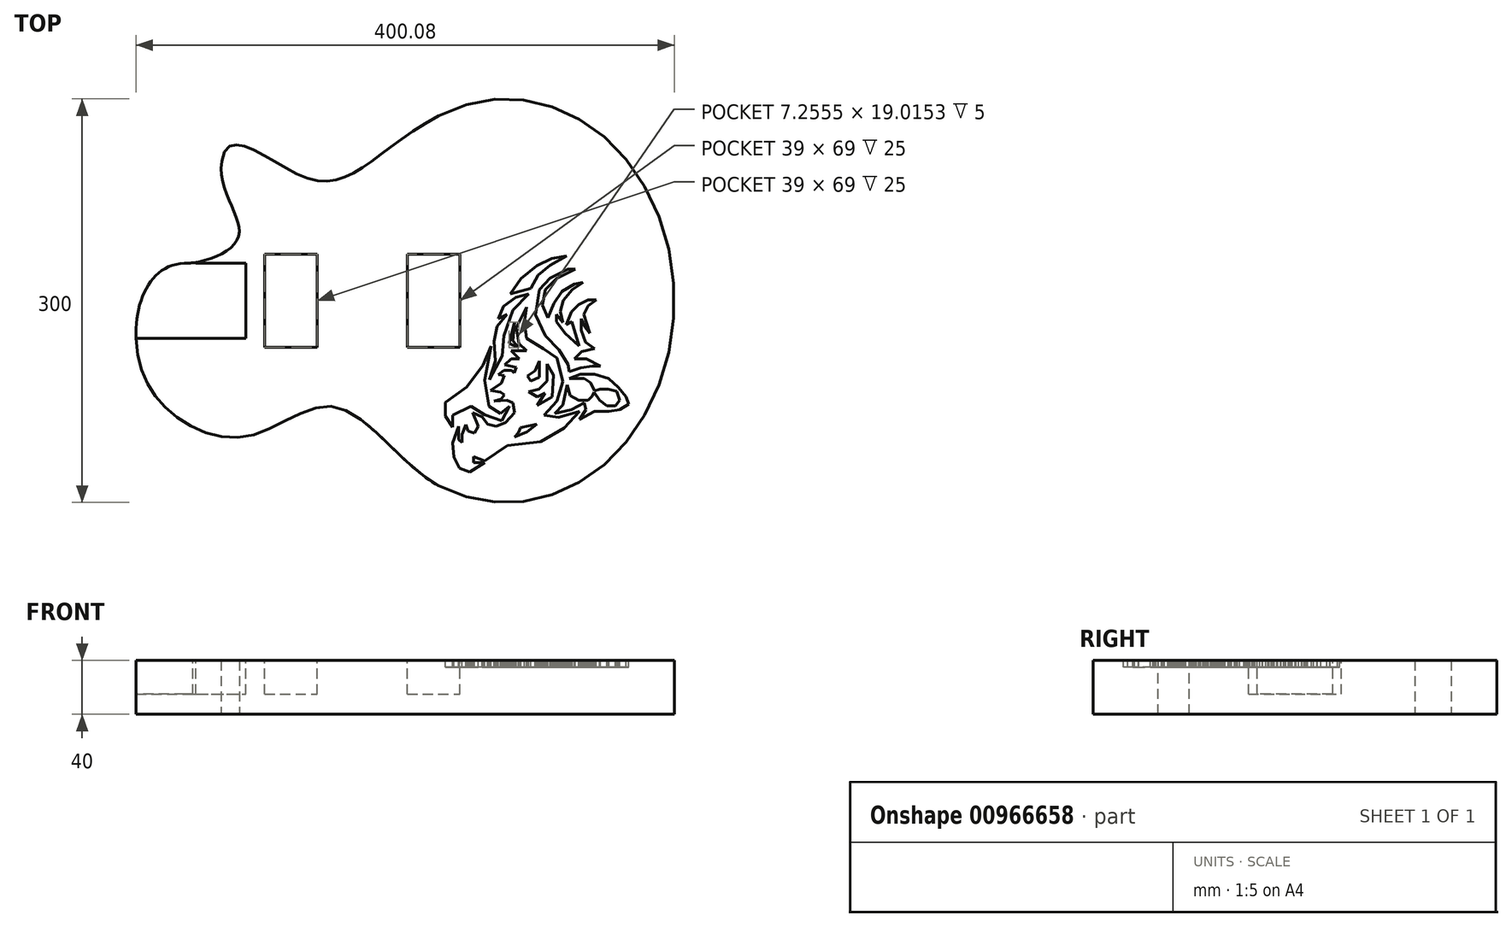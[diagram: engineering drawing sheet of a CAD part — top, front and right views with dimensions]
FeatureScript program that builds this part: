
annotation { "Feature Type Name" : "Feature", "Feature Type Description" : "" }
export const myFeature = defineFeature(function(context is Context, id is Id, definition is map)
    precondition{}
    {
        {
            var Q0;
            Q0=qCreatedBy(makeId("Top.planeOp"),FACE);
            var sketch = newSketch(context, id + "F0", { "sketchPlane" : qUnion([Q0])});
            skLineSegment(sketch, "E0.right", {"start": v(-149.13, 58.2) * mm, "end": v(-149.13, 58.2) * mm});
            skPoint(sketch, "E0.middle", {"position": v(0, 0) * mm});
            skEllipticalArc(sketch, "E1", {});
            skFitSpline(sketch, "E2", {"points": [v(0, 137.5) * mm, v(-96.85, 90.92) * mm, v(-161.22, 103.65) * mm], "startDerivative": vector(-241.63, -126.18) * mm, "endDerivative": vector(-31.25, -209.57) * mm});
            skFitSpline(sketch, "E3", {"points": [v(-161.22, 103.65) * mm, v(-148.55, 48.3) * mm, v(-188.99, 27.75) * mm], "startDerivative": vector(-19.02, -127.57) * mm, "endDerivative": vector(-101.56, -1.92) * mm});
            skFitSpline(sketch, "E4", {"points": [v(0, -137.5) * mm, v(-77.16, -78.98) * mm, v(-142.06, -100.85) * mm, v(-201.85, -80.43) * mm, v(-224.87, -27.75) * mm], "startDerivative": vector(-279.2, 145.79) * mm, "endDerivative": vector(-12.82, 299.13) * mm});
            skFitSpline(sketch, "E5", {"points": [v(-188.99, 27.75) * mm, v(-224.87, -27.75) * mm], "startDerivative": vector(-74.02, -1.4) * mm, "endDerivative": vector(3.57, -83.25) * mm});
            skPoint(sketch, "E6", {"position": v(175.13, 0) * mm});
            const initialGuessF0  = {"E1": [0.05, 0, 1, 0, 0.125128804762181, 0.15, 4.301321347421228, 1.9818639597583554]};
            skSetInitialGuess(sketch, initialGuessF0);
            skSolve(sketch);
        }
        {
            var Q0;
            Q0 = qSketchRegion(id + "F0", true);
            extrude(context, id + "F1", {"entities" : qUnion([Q0]), "oppositeDirection" : true, "depth" : 40 * mm, "offsetDistance" : 25 * mm});
        }
        {
            var Q0;
            Q0=qCreatedBy(makeId("Top.planeOp"),FACE);
            var sketch = newSketch(context, id + "F2", { "sketchPlane" : qUnion([Q0])});
            skLineSegment(sketch, "E7", {"start": v(34.15, -120.48) * mm, "end": v(25.86, -120.48) * mm});
            skLineSegment(sketch, "E8", {"start": v(25.86, -120.48) * mm, "end": v(25.86, -115.9) * mm});
            skLineSegment(sketch, "E9", {"start": v(25.86, -115.9) * mm, "end": v(34.15, -119.08) * mm});
            skLineSegment(sketch, "E10", {"start": v(34.15, -119.08) * mm, "end": v(51.15, -107.54) * mm});
            skLineSegment(sketch, "E11", {"start": v(51.15, -107.54) * mm, "end": v(75.76, -104.73) * mm});
            skLineSegment(sketch, "E12", {"start": v(75.76, -104.73) * mm, "end": v(93.08, -94.6) * mm});
            skLineSegment(sketch, "E13", {"start": v(93.08, -94.6) * mm, "end": v(104.6, -82.3) * mm});
            skLineSegment(sketch, "E14", {"start": v(104.6, -82.3) * mm, "end": v(89.1, -86.85) * mm});
            skLineSegment(sketch, "E15", {"start": v(89.1, -86.85) * mm, "end": v(78.2, -85.15) * mm});
            skLineSegment(sketch, "E16", {"start": v(78.2, -85.15) * mm, "end": v(87.98, -74.8) * mm});
            skLineSegment(sketch, "E17", {"start": v(87.98, -74.8) * mm, "end": v(92.17, -60.06) * mm});
            skLineSegment(sketch, "E18", {"start": v(92.17, -60.06) * mm, "end": v(87.98, -42.56) * mm});
            skLineSegment(sketch, "E19", {"start": v(87.98, -42.56) * mm, "end": v(77.6, -35.69) * mm});
            skLineSegment(sketch, "E20", {"start": v(77.6, -35.69) * mm, "end": v(65.34, -28.13) * mm});
            skLineSegment(sketch, "E21", {"start": v(65.34, -28.13) * mm, "end": v(63.85, -15.98) * mm});
            skLineSegment(sketch, "E22", {"start": v(63.85, -15.98) * mm, "end": v(65.34, -4.86) * mm});
            skLineSegment(sketch, "E23", {"start": v(65.34, -4.86) * mm, "end": v(57.6, -20.1) * mm});
            skLineSegment(sketch, "E24", {"start": v(57.6, -20.1) * mm, "end": v(59.45, -31.88) * mm});
            skLineSegment(sketch, "E25", {"start": v(59.45, -31.88) * mm, "end": v(65.34, -37.21) * mm});
            skLineSegment(sketch, "E26", {"start": v(65.34, -37.21) * mm, "end": v(53.96, -37.21) * mm});
            skLineSegment(sketch, "E27", {"start": v(53.96, -37.21) * mm, "end": v(59.8, -43.34) * mm});
            skLineSegment(sketch, "E28", {"start": v(59.8, -43.34) * mm, "end": v(53.95, -43.34) * mm});
            skLineSegment(sketch, "E29", {"start": v(53.95, -43.34) * mm, "end": v(49.16, -47.6) * mm});
            skLineSegment(sketch, "E30", {"start": v(49.16, -47.6) * mm, "end": v(57.6, -49.5) * mm});
            skLineSegment(sketch, "E31", {"start": v(57.6, -49.5) * mm, "end": v(56.04, -53.58) * mm});
            skLineSegment(sketch, "E32", {"start": v(56.04, -53.58) * mm, "end": v(54.25, -51.86) * mm});
            skLineSegment(sketch, "E33", {"start": v(54.25, -51.86) * mm, "end": v(48.56, -51.86) * mm});
            skLineSegment(sketch, "E34", {"start": v(48.56, -51.86) * mm, "end": v(44.36, -55.11) * mm});
            skLineSegment(sketch, "E35", {"start": v(44.36, -55.11) * mm, "end": v(48.68, -55.7) * mm});
            skLineSegment(sketch, "E36", {"start": v(48.68, -55.7) * mm, "end": v(46.5, -61.35) * mm});
            skLineSegment(sketch, "E37", {"start": v(46.5, -61.35) * mm, "end": v(38.66, -66.84) * mm});
            skLineSegment(sketch, "E38", {"start": v(38.66, -66.84) * mm, "end": v(46.08, -67.84) * mm});
            skLineSegment(sketch, "E39", {"start": v(46.08, -67.84) * mm, "end": v(48.9, -69.92) * mm});
            skLineSegment(sketch, "E40", {"start": v(48.9, -69.92) * mm, "end": v(46.46, -73.2) * mm});
            skLineSegment(sketch, "E41", {"start": v(46.46, -73.2) * mm, "end": v(41.01, -74.8) * mm});
            skLineSegment(sketch, "E42", {"start": v(41.01, -74.8) * mm, "end": v(50.8, -74.08) * mm});
            skLineSegment(sketch, "E43", {"start": v(50.8, -74.08) * mm, "end": v(55.2, -75.77) * mm});
            skLineSegment(sketch, "E44", {"start": v(55.2, -75.77) * mm, "end": v(56.32, -83.2) * mm});
            skLineSegment(sketch, "E45", {"start": v(56.32, -83.2) * mm, "end": v(49.77, -90.5) * mm});
            skLineSegment(sketch, "E46", {"start": v(49.77, -90.5) * mm, "end": v(42.78, -93.37) * mm});
            skLineSegment(sketch, "E47", {"start": v(42.78, -93.37) * mm, "end": v(36.34, -91.87) * mm});
            skLineSegment(sketch, "E48", {"start": v(36.34, -91.87) * mm, "end": v(32.35, -86.32) * mm});
            skLineSegment(sketch, "E49", {"start": v(32.35, -86.32) * mm, "end": v(25.42, -83.37) * mm});
            skLineSegment(sketch, "E50", {"start": v(25.42, -83.37) * mm, "end": v(29.3, -93.37) * mm});
            skLineSegment(sketch, "E51", {"start": v(29.3, -93.37) * mm, "end": v(26.6, -98.34) * mm});
            skLineSegment(sketch, "E52", {"start": v(26.6, -98.34) * mm, "end": v(21.8, -96.98) * mm});
            skLineSegment(sketch, "E53", {"start": v(21.8, -96.98) * mm, "end": v(20.08, -92.2) * mm});
            skLineSegment(sketch, "E54", {"start": v(20.08, -92.2) * mm, "end": v(17.32, -99.34) * mm});
            skLineSegment(sketch, "E55", {"start": v(17.32, -99.34) * mm, "end": v(17.32, -105.35) * mm});
            skLineSegment(sketch, "E56", {"start": v(17.32, -105.35) * mm, "end": v(14.69, -103.3) * mm});
            skLineSegment(sketch, "E57", {"start": v(14.69, -103.3) * mm, "end": v(14.69, -93.37) * mm});
            skLineSegment(sketch, "E58", {"start": v(14.69, -93.37) * mm, "end": v(10.4, -105.66) * mm});
            skLineSegment(sketch, "E59", {"start": v(10.4, -105.66) * mm, "end": v(11.23, -116.37) * mm});
            skLineSegment(sketch, "E60", {"start": v(11.23, -116.37) * mm, "end": v(15.54, -124.36) * mm});
            skLineSegment(sketch, "E61", {"start": v(15.54, -124.36) * mm, "end": v(22.96, -127.5) * mm});
            skLineSegment(sketch, "E62", {"start": v(34.15, -120.48) * mm, "end": v(22.96, -127.5) * mm});
            skLineSegment(sketch, "E63", {"start": v(56.36, -101.4) * mm, "end": v(65.78, -97.66) * mm});
            skLineSegment(sketch, "E64", {"start": v(65.78, -97.66) * mm, "end": v(72.9, -91.7) * mm});
            skLineSegment(sketch, "E65", {"start": v(72.9, -91.7) * mm, "end": v(60.84, -94.3) * mm});
            skLineSegment(sketch, "E66", {"start": v(60.84, -94.3) * mm, "end": v(59.37, -98.15) * mm});
            skLineSegment(sketch, "E67", {"start": v(59.37, -98.15) * mm, "end": v(56.36, -101.4) * mm});
            skLineSegment(sketch, "E68", {"start": v(86.2, -83.8) * mm, "end": v(92.41, -77.5) * mm});
            skLineSegment(sketch, "E69", {"start": v(92.41, -77.5) * mm, "end": v(95.48, -62.62) * mm});
            skLineSegment(sketch, "E70", {"start": v(95.48, -62.62) * mm, "end": v(97.84, -70.66) * mm});
            skLineSegment(sketch, "E71", {"start": v(97.84, -70.66) * mm, "end": v(104, -73.9) * mm});
            skLineSegment(sketch, "E72", {"start": v(104, -73.9) * mm, "end": v(110.96, -73.9) * mm});
            skLineSegment(sketch, "E73", {"start": v(110.96, -73.9) * mm, "end": v(114.16, -70.96) * mm});
            skLineSegment(sketch, "E74", {"start": v(114.16, -70.96) * mm, "end": v(115.46, -68.12) * mm});
            skLineSegment(sketch, "E75", {"start": v(115.46, -68.12) * mm, "end": v(119.55, -73.9) * mm});
            skLineSegment(sketch, "E76", {"start": v(119.55, -73.9) * mm, "end": v(124.87, -78.28) * mm});
            skLineSegment(sketch, "E77", {"start": v(124.87, -78.28) * mm, "end": v(131.2, -78.28) * mm});
            skLineSegment(sketch, "E78", {"start": v(131.2, -78.28) * mm, "end": v(134.45, -73.9) * mm});
            skLineSegment(sketch, "E79", {"start": v(134.45, -73.9) * mm, "end": v(132.34, -67.32) * mm});
            skLineSegment(sketch, "E80", {"start": v(132.34, -67.32) * mm, "end": v(126.07, -65.63) * mm});
            skLineSegment(sketch, "E81", {"start": v(126.07, -65.63) * mm, "end": v(119.83, -65.63) * mm});
            skLineSegment(sketch, "E82", {"start": v(119.83, -65.63) * mm, "end": v(115.8, -66.93) * mm});
            skLineSegment(sketch, "E83", {"start": v(115.8, -66.93) * mm, "end": v(113.06, -60.9) * mm});
            skLineSegment(sketch, "E84", {"start": v(113.06, -60.9) * mm, "end": v(108.13, -57.9) * mm});
            skLineSegment(sketch, "E85", {"start": v(108.13, -57.9) * mm, "end": v(96.94, -57.9) * mm});
            skLineSegment(sketch, "E86", {"start": v(96.94, -57.9) * mm, "end": v(105.18, -54.7) * mm});
            skLineSegment(sketch, "E87", {"start": v(105.18, -54.7) * mm, "end": v(115.65, -54.7) * mm});
            skLineSegment(sketch, "E88", {"start": v(115.65, -54.7) * mm, "end": v(126.11, -57.9) * mm});
            skLineSegment(sketch, "E89", {"start": v(126.11, -57.9) * mm, "end": v(133.55, -64.57) * mm});
            skLineSegment(sketch, "E90", {"start": v(133.55, -64.57) * mm, "end": v(139.38, -71.53) * mm});
            skLineSegment(sketch, "E91", {"start": v(139.38, -71.53) * mm, "end": v(141.1, -76.77) * mm});
            skLineSegment(sketch, "E92", {"start": v(141.1, -76.77) * mm, "end": v(134.5, -81) * mm});
            skLineSegment(sketch, "E93", {"start": v(134.5, -81) * mm, "end": v(126.48, -82.15) * mm});
            skLineSegment(sketch, "E94", {"start": v(126.48, -82.15) * mm, "end": v(115.65, -82.15) * mm});
            skLineSegment(sketch, "E95", {"start": v(115.65, -82.15) * mm, "end": v(104.72, -88.23) * mm});
            skLineSegment(sketch, "E96", {"start": v(104.72, -88.23) * mm, "end": v(109.47, -81.05) * mm});
            skLineSegment(sketch, "E97", {"start": v(109.47, -81.05) * mm, "end": v(108.2, -75.8) * mm});
            skLineSegment(sketch, "E98", {"start": v(108.2, -75.8) * mm, "end": v(98.54, -81.1) * mm});
            skLineSegment(sketch, "E99", {"start": v(98.54, -81.1) * mm, "end": v(86.2, -83.8) * mm});
            skLineSegment(sketch, "E100", {"start": v(96.94, -52.87) * mm, "end": v(105.54, -49.79) * mm});
            skLineSegment(sketch, "E101", {"start": v(105.54, -49.79) * mm, "end": v(114.19, -48.52) * mm});
            skLineSegment(sketch, "E102", {"start": v(114.19, -48.52) * mm, "end": v(120.34, -48.52) * mm});
            skLineSegment(sketch, "E103", {"start": v(120.34, -48.52) * mm, "end": v(109.75, -43.16) * mm});
            skLineSegment(sketch, "E104", {"start": v(109.75, -43.16) * mm, "end": v(100.9, -43.16) * mm});
            skLineSegment(sketch, "E105", {"start": v(100.9, -43.16) * mm, "end": v(106.16, -37.82) * mm});
            skLineSegment(sketch, "E106", {"start": v(106.16, -37.82) * mm, "end": v(115.65, -35.51) * mm});
            skLineSegment(sketch, "E107", {"start": v(115.65, -35.51) * mm, "end": v(109.24, -30.81) * mm});
            skLineSegment(sketch, "E108", {"start": v(109.24, -30.81) * mm, "end": v(106.1, -21.8) * mm});
            skLineSegment(sketch, "E109", {"start": v(106.1, -21.8) * mm, "end": v(106.1, -13.36) * mm});
            skLineSegment(sketch, "E110", {"start": v(106.1, -13.36) * mm, "end": v(108.95, -19.83) * mm});
            skLineSegment(sketch, "E111", {"start": v(108.95, -19.83) * mm, "end": v(112.19, -24.03) * mm});
            skLineSegment(sketch, "E112", {"start": v(112.19, -24.03) * mm, "end": v(107.95, -10.3) * mm});
            skLineSegment(sketch, "E113", {"start": v(107.95, -10.3) * mm, "end": v(110.96, -3.8) * mm});
            skLineSegment(sketch, "E114", {"start": v(110.96, -3.8) * mm, "end": v(116.96, 0.69) * mm});
            skLineSegment(sketch, "E115", {"start": v(116.96, 0.69) * mm, "end": v(110.96, 0.69) * mm});
            skLineSegment(sketch, "E116", {"start": v(110.96, 0.69) * mm, "end": v(104.02, -2.85) * mm});
            skLineSegment(sketch, "E117", {"start": v(104.02, -2.85) * mm, "end": v(98.67, -8.29) * mm});
            skLineSegment(sketch, "E118", {"start": v(98.67, -8.29) * mm, "end": v(94.72, -17.67) * mm});
            skLineSegment(sketch, "E119", {"start": v(94.72, -17.67) * mm, "end": v(98.84, -15.5) * mm});
            skLineSegment(sketch, "E120", {"start": v(98.84, -15.5) * mm, "end": v(104.33, -33.55) * mm});
            skLineSegment(sketch, "E121", {"start": v(104.33, -33.55) * mm, "end": v(93.85, -24.32) * mm});
            skLineSegment(sketch, "E122", {"start": v(93.85, -24.32) * mm, "end": v(87.45, -15.63) * mm});
            skLineSegment(sketch, "E123", {"start": v(87.45, -15.63) * mm, "end": v(87.45, -10.28) * mm});
            skLineSegment(sketch, "E124", {"start": v(87.45, -10.28) * mm, "end": v(92.44, -16.35) * mm});
            skLineSegment(sketch, "E125", {"start": v(92.44, -16.35) * mm, "end": v(90.43, -8.1) * mm});
            skLineSegment(sketch, "E126", {"start": v(90.43, -8.1) * mm, "end": v(92.58, 0.19) * mm});
            skLineSegment(sketch, "E127", {"start": v(92.58, 0.19) * mm, "end": v(99.1, 8.32) * mm});
            skLineSegment(sketch, "E128", {"start": v(99.1, 8.32) * mm, "end": v(107.32, 13.75) * mm});
            skLineSegment(sketch, "E129", {"start": v(107.32, 13.75) * mm, "end": v(100.9, 12.2) * mm});
            skLineSegment(sketch, "E130", {"start": v(100.9, 12.2) * mm, "end": v(91.64, 6.8) * mm});
            skLineSegment(sketch, "E131", {"start": v(91.64, 6.8) * mm, "end": v(85.57, -1.95) * mm});
            skLineSegment(sketch, "E132", {"start": v(85.57, -1.95) * mm, "end": v(81.26, -12.76) * mm});
            skLineSegment(sketch, "E133", {"start": v(81.26, -12.76) * mm, "end": v(77, -3.13) * mm});
            skLineSegment(sketch, "E134", {"start": v(77, -3.13) * mm, "end": v(79.14, 8.18) * mm});
            skLineSegment(sketch, "E135", {"start": v(79.14, 8.18) * mm, "end": v(87.39, 16.52) * mm});
            skLineSegment(sketch, "E136", {"start": v(87.39, 16.52) * mm, "end": v(101.35, 23.53) * mm});
            skLineSegment(sketch, "E137", {"start": v(101.35, 23.53) * mm, "end": v(96.2, 23.53) * mm});
            skLineSegment(sketch, "E138", {"start": v(96.2, 23.53) * mm, "end": v(82.87, 16.7) * mm});
            skLineSegment(sketch, "E139", {"start": v(82.87, 16.7) * mm, "end": v(74.72, 8.27) * mm});
            skLineSegment(sketch, "E140", {"start": v(74.72, 8.27) * mm, "end": v(72.09, -10.5) * mm});
            skLineSegment(sketch, "E141", {"start": v(72.09, -10.5) * mm, "end": v(79.16, -26.04) * mm});
            skLineSegment(sketch, "E142", {"start": v(79.16, -26.04) * mm, "end": v(89.39, -36.67) * mm});
            skLineSegment(sketch, "E143", {"start": v(89.39, -36.67) * mm, "end": v(96.1, -47.25) * mm});
            skLineSegment(sketch, "E144", {"start": v(96.1, -47.25) * mm, "end": v(96.94, -52.87) * mm});
            skLineSegment(sketch, "E145", {"start": v(68.64, 9.33) * mm, "end": v(73.79, 19.06) * mm});
            skLineSegment(sketch, "E146", {"start": v(73.79, 19.06) * mm, "end": v(82.87, 26.24) * mm});
            skLineSegment(sketch, "E147", {"start": v(82.87, 26.24) * mm, "end": v(95.3, 33.31) * mm});
            skLineSegment(sketch, "E148", {"start": v(95.3, 33.31) * mm, "end": v(83.96, 31.53) * mm});
            skLineSegment(sketch, "E149", {"start": v(83.96, 31.53) * mm, "end": v(72.85, 25.95) * mm});
            skLineSegment(sketch, "E150", {"start": v(72.85, 25.95) * mm, "end": v(61.28, 16.44) * mm});
            skLineSegment(sketch, "E151", {"start": v(61.28, 16.44) * mm, "end": v(53.18, 5.2) * mm});
            skLineSegment(sketch, "E152", {"start": v(53.18, 5.2) * mm, "end": v(68.64, 9.33) * mm});
            skLineSegment(sketch, "E153", {"start": v(66.92, 4.93) * mm, "end": v(57.21, 2.57) * mm});
            skLineSegment(sketch, "E154", {"start": v(57.21, 2.57) * mm, "end": v(48.2, -4.17) * mm});
            skLineSegment(sketch, "E155", {"start": v(48.2, -4.17) * mm, "end": v(44.34, -13.37) * mm});
            skLineSegment(sketch, "E156", {"start": v(44.34, -13.37) * mm, "end": v(50.57, -10.28) * mm});
            skLineSegment(sketch, "E157", {"start": v(50.57, -10.28) * mm, "end": v(43.25, -19.17) * mm});
            skLineSegment(sketch, "E158", {"start": v(43.25, -19.17) * mm, "end": v(41.2, -30.04) * mm});
            skLineSegment(sketch, "E159", {"start": v(41.2, -30.04) * mm, "end": v(42.1, -44.73) * mm});
            skLineSegment(sketch, "E160", {"start": v(42.1, -44.73) * mm, "end": v(37.76, -58.62) * mm});
            skLineSegment(sketch, "E161", {"start": v(37.76, -58.62) * mm, "end": v(47.36, -41.07) * mm});
            skLineSegment(sketch, "E162", {"start": v(47.36, -41.07) * mm, "end": v(48.35, -26.04) * mm});
            skLineSegment(sketch, "E163", {"start": v(48.35, -26.04) * mm, "end": v(55.03, -6.94) * mm});
            skLineSegment(sketch, "E164", {"start": v(55.03, -6.94) * mm, "end": v(66.92, 4.93) * mm});
            skLineSegment(sketch, "E165", {"start": v(59.54, -34.92) * mm, "end": v(52.28, -31.87) * mm});
            skLineSegment(sketch, "E166", {"start": v(52.28, -31.87) * mm, "end": v(56.47, -15.9) * mm});
            skLineSegment(sketch, "E167", {"start": v(56.47, -15.9) * mm, "end": v(55.1, -29.83) * mm});
            skLineSegment(sketch, "E168", {"start": v(55.1, -29.83) * mm, "end": v(59.54, -34.92) * mm});
            skLineSegment(sketch, "E169", {"start": v(39.09, -33.55) * mm, "end": v(34.26, -59.14) * mm});
            skLineSegment(sketch, "E170", {"start": v(34.26, -59.14) * mm, "end": v(37.27, -78.34) * mm});
            skLineSegment(sketch, "E171", {"start": v(37.27, -78.34) * mm, "end": v(46.07, -83.77) * mm});
            skLineSegment(sketch, "E172", {"start": v(46.07, -83.77) * mm, "end": v(52.5, -78.58) * mm});
            skLineSegment(sketch, "E173", {"start": v(52.5, -78.58) * mm, "end": v(46.92, -89.32) * mm});
            skLineSegment(sketch, "E174", {"start": v(46.92, -89.32) * mm, "end": v(34.28, -84.86) * mm});
            skLineSegment(sketch, "E175", {"start": v(34.28, -84.86) * mm, "end": v(23.95, -78.48) * mm});
            skLineSegment(sketch, "E176", {"start": v(23.95, -78.48) * mm, "end": v(10.43, -85.26) * mm});
            skLineSegment(sketch, "E177", {"start": v(10.43, -85.26) * mm, "end": v(10.43, -93.9) * mm});
            skLineSegment(sketch, "E178", {"start": v(10.43, -93.9) * mm, "end": v(5.1, -85.64) * mm});
            skLineSegment(sketch, "E179", {"start": v(5.1, -85.64) * mm, "end": v(5.1, -75.73) * mm});
            skLineSegment(sketch, "E180", {"start": v(5.1, -75.73) * mm, "end": v(20.88, -64.24) * mm});
            skLineSegment(sketch, "E181", {"start": v(20.88, -64.24) * mm, "end": v(32.77, -47.91) * mm});
            skLineSegment(sketch, "E182", {"start": v(32.77, -47.91) * mm, "end": v(39.09, -33.55) * mm});
            skLineSegment(sketch, "E183", {"start": v(68.64, -59.76) * mm, "end": v(65.98, -55.9) * mm});
            skLineSegment(sketch, "E184", {"start": v(65.98, -55.9) * mm, "end": v(71.66, -51.98) * mm});
            skLineSegment(sketch, "E185", {"start": v(71.66, -51.98) * mm, "end": v(74.69, -44.79) * mm});
            skLineSegment(sketch, "E186", {"start": v(74.69, -44.79) * mm, "end": v(74.69, -57) * mm});
            skLineSegment(sketch, "E187", {"start": v(74.69, -57) * mm, "end": v(68.64, -59.76) * mm});
            skLineSegment(sketch, "E188", {"start": v(66.92, -67.68) * mm, "end": v(73.2, -71.56) * mm});
            skLineSegment(sketch, "E189", {"start": v(73.2, -71.56) * mm, "end": v(78.87, -68.54) * mm});
            skLineSegment(sketch, "E190", {"start": v(78.87, -68.54) * mm, "end": v(73.11, -77.86) * mm});
            skLineSegment(sketch, "E191", {"start": v(73.11, -77.86) * mm, "end": v(84.52, -71.33) * mm});
            skLineSegment(sketch, "E192", {"start": v(84.52, -71.33) * mm, "end": v(85.4, -55.14) * mm});
            skLineSegment(sketch, "E193", {"start": v(85.4, -55.14) * mm, "end": v(80.54, -47.06) * mm});
            skLineSegment(sketch, "E194", {"start": v(80.54, -47.06) * mm, "end": v(80.54, -59.76) * mm});
            skLineSegment(sketch, "E195", {"start": v(80.54, -59.76) * mm, "end": v(74.39, -65.81) * mm});
            skLineSegment(sketch, "E196", {"start": v(74.39, -65.81) * mm, "end": v(66.92, -67.68) * mm});
            skSolve(sketch);
        }
        {
            var Q0;
            Q0 = qSketchRegion(id + "F2", true);
            extrude(context, id + "F3", {"entities" : qUnion([Q0]), "operationType" : NewBodyOperationType.REMOVE, "oppositeDirection" : true, "depth" : 5 * mm, "offsetDistance" : 25 * mm});
        }
        {
            var Q0;
            Q0=qCreatedBy(makeId("Top.planeOp"),FACE);
            var sketch = newSketch(context, id + "F4", { "sketchPlane" : qUnion([Q0])});
            skLineSegment(sketch, "E197", {"start": v(-233.49, -28) * mm, "end": v(-143.3, -28) * mm});
            skLineSegment(sketch, "E198", {"start": v(-180.6, 28) * mm, "end": v(-143.3, 28) * mm});
            skLineSegment(sketch, "E199", {"start": v(-143.3, 28) * mm, "end": v(-143.3, -28) * mm});
            skLineSegment(sketch, "E200.bottom", {"start": v(-129.3, 34.5) * mm, "end": v(-90.3, 34.5) * mm});
            skLineSegment(sketch, "E200.top", {"start": v(-129.3, -34.5) * mm, "end": v(-90.3, -34.5) * mm});
            skLineSegment(sketch, "E200.left", {"start": v(-129.3, 34.5) * mm, "end": v(-129.3, -34.5) * mm});
            skLineSegment(sketch, "E200.right", {"start": v(-90.3, 34.5) * mm, "end": v(-90.3, -34.5) * mm});
            skPoint(sketch, "E200.middle", {"position": v(-109.8, 0) * mm});
            skLineSegment(sketch, "E201.bottom", {"start": v(-23.3, -34.5) * mm, "end": v(15.7, -34.5) * mm});
            skLineSegment(sketch, "E201.top", {"start": v(-23.3, 34.5) * mm, "end": v(15.7, 34.5) * mm});
            skLineSegment(sketch, "E201.left", {"start": v(-23.3, -34.5) * mm, "end": v(-23.3, 34.5) * mm});
            skLineSegment(sketch, "E201.right", {"start": v(15.7, -34.5) * mm, "end": v(15.7, 34.5) * mm});
            skPoint(sketch, "E201.middle", {"position": v(-3.8, 0) * mm});
            skLineSegment(sketch, "E202", {"start": v(-233.49, -28) * mm, "end": v(-250.72, 35.95) * mm});
            skLineSegment(sketch, "E203", {"start": v(-250.72, 35.95) * mm, "end": v(-180.6, 28) * mm});
            skSolve(sketch);
        }
        {
            var Q0;
            Q0 = qSketchRegion(id + "F4", true);
            extrude(context, id + "F5", {"entities" : qUnion([Q0]), "operationType" : NewBodyOperationType.REMOVE, "oppositeDirection" : true, "depth" : 25 * mm, "offsetDistance" : 25 * mm});
        }
    });
